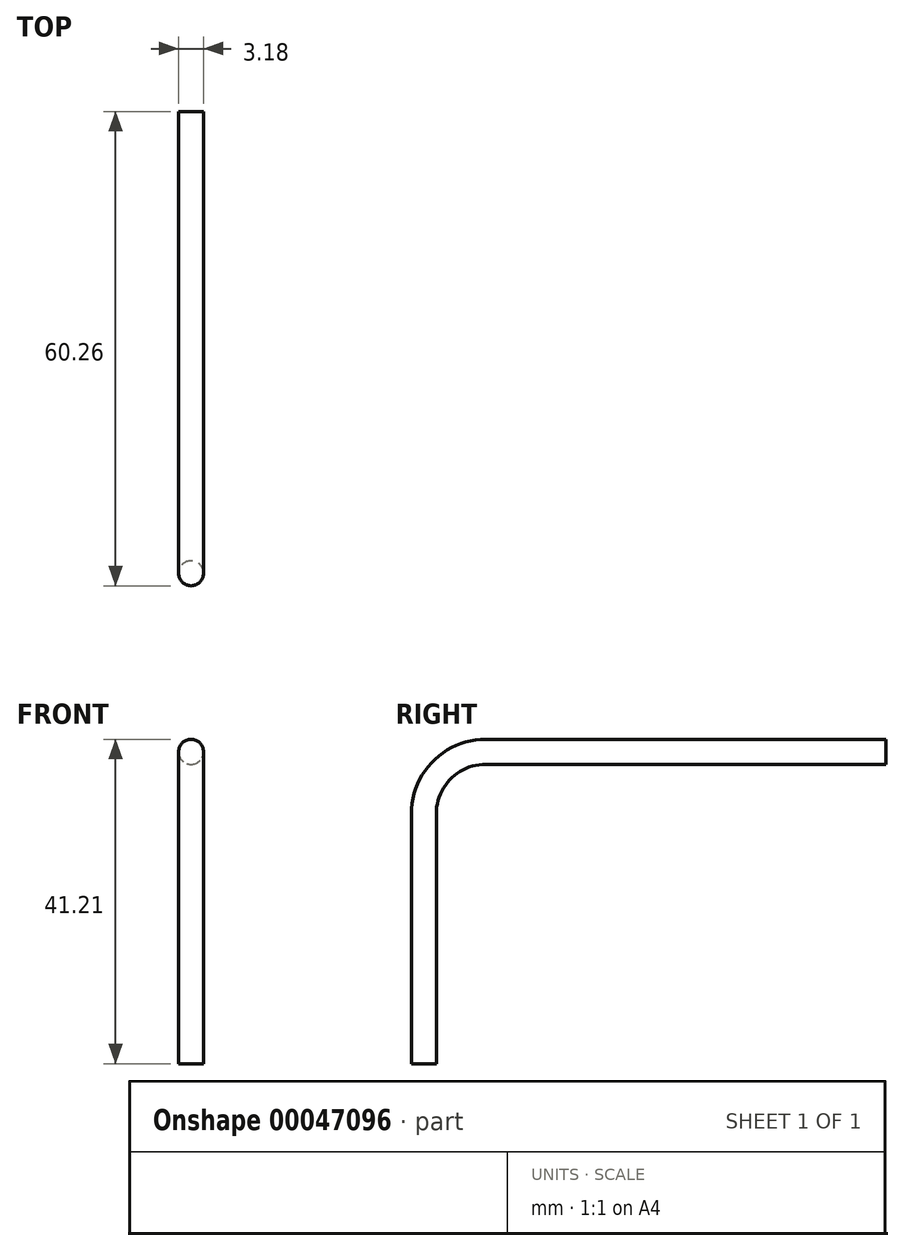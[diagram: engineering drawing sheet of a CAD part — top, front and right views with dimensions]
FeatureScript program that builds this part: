
annotation { "Feature Type Name" : "Feature", "Feature Type Description" : "" }
export const myFeature = defineFeature(function(context is Context, id is Id, definition is map)
    precondition{}
    {
        {
            var Q0;
            Q0=qCreatedBy(makeId("Right.planeOp"),FACE);
            var sketch = newSketch(context, id + "F0", { "sketchPlane" : qUnion([Q0])});
            skLineSegment(sketch, "E0", {"start": v(0, -39.62) * mm, "end": v(0, -7.87) * mm});
            skArc(sketch, "E1", {"start": v(7.87, 0) * mm, "mid": v(2.3, -2.3) * mm, "end": v(0, -7.87) * mm});
            skLineSegment(sketch, "E2", {"start": v(7.87, 0) * mm, "end": v(58.67, 0) * mm});
            skSolve(sketch);
        }
        {
            var Q0;
            Q0=sQuery(id+"F0.wireOp",VERTEX,"E0.start");
            var Q1;
            Q1=qCreatedBy(makeId("Top.planeOp"),FACE);
            cPlane(context, id + "F1", {"entities" : qUnion([Q0, Q1]), "cplaneType" : CPlaneType.PLANE_POINT, "offset" : 152.4 * mm, "width" : 152.4 * mm, "height" : 152.4 * mm});
        }
        {
            var Q0;
            Q0=qCreatedBy(id+"F1.planeOp",FACE);
            var sketch = newSketch(context, id + "F2", { "sketchPlane" : qUnion([Q0])});
            skCircle(sketch, "E3", {"center": v(0, 0) * mm, "radius": 1.59 * mm});
            skSolve(sketch);
        }
        {
            var Q0;
            Q0=makeQuery(id+"F2.imprint","IMPRINT",FACE,{"disambiguationData":[TD([[makeQuery(id+"F2.imprint","IMPRINT",EDGE,{"derivedFrom":sQuery(id+"F2.wireOp",EDGE,"E3")}),1.0]])]});
            var Q1;
            Q1 = qConstructionFilter(qBodyType(qCreatedBy(id + "F0" ,EDGE), BodyType.WIRE), ConstructionObject.NO);
            sweep(context, id + "F3", {"profiles" : qUnion([Q0]), "path" : qUnion([Q1])});
        }
    });
